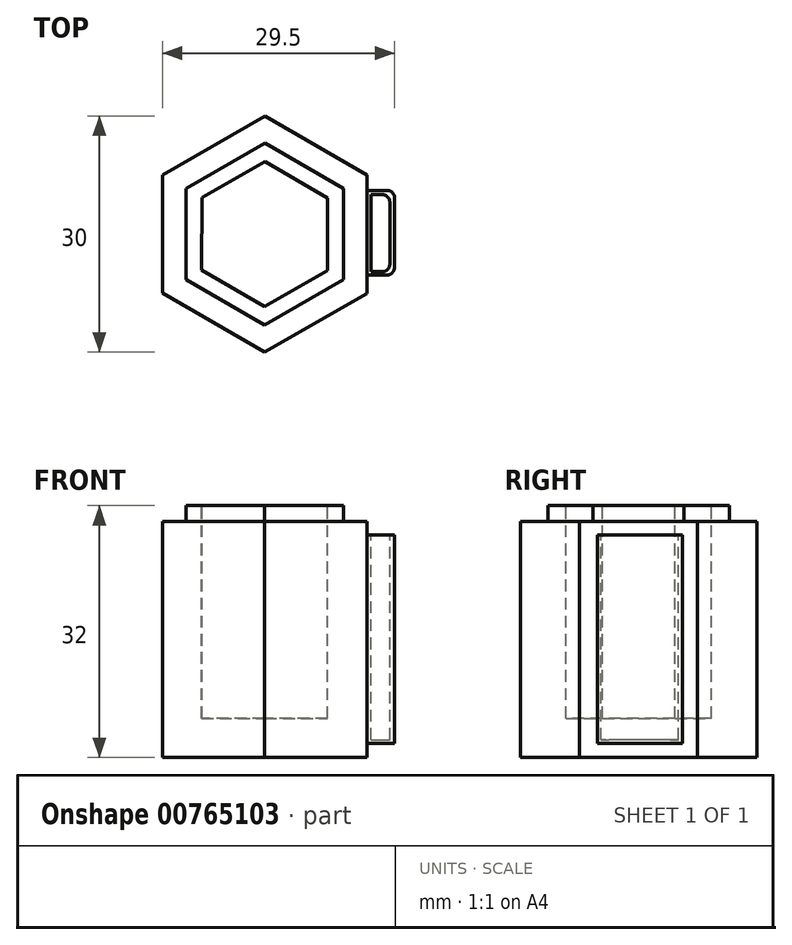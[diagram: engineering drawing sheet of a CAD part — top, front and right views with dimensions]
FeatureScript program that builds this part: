
annotation { "Feature Type Name" : "Feature", "Feature Type Description" : "" }
export const myFeature = defineFeature(function(context is Context, id is Id, definition is map)
    precondition{}
    {
        {
            var Q0;
            Q0=qCreatedBy(makeId("Top.planeOp"),FACE);
            var sketch = newSketch(context, id + "F0", { "sketchPlane" : qUnion([Q0])});
            skCircle(sketch, "E0.cCircle", {"center": v(0, 0) * mm, "radius": 13 * mm, "construction": true});
            skLineSegment(sketch, "E0.0", {"start": v(0.03, 15) * mm, "end": v(13, 7.48) * mm});
            skLineSegment(sketch, "E0.1", {"start": v(13, 7.48) * mm, "end": v(12.98, -7.52) * mm});
            skLineSegment(sketch, "E0.2", {"start": v(12.98, -7.52) * mm, "end": v(-0.03, -15) * mm});
            skLineSegment(sketch, "E0.3", {"start": v(-0.03, -15) * mm, "end": v(-13, -7.48) * mm});
            skLineSegment(sketch, "E0.4", {"start": v(-13, -7.48) * mm, "end": v(-12.98, 7.52) * mm});
            skLineSegment(sketch, "E0.5", {"start": v(-12.98, 7.52) * mm, "end": v(0.03, 15) * mm});
            skPoint(sketch, "E0.0.midPoint", {"position": v(6.52, 11.24) * mm});
            skSolve(sketch);
        }
        {
            var Q0;
            Q0=makeQuery(id+"F0.imprint","IMPRINT",FACE,{"disambiguationData":[TD([[makeQuery(id+"F0.imprint","IMPRINT",EDGE,{"derivedFrom":sQuery(id+"F0.wireOp",EDGE,"E0.0")}),-1.0]])]});
            extrude(context, id + "F1", {"entities" : qUnion([Q0]), "oppositeDirection" : true, "depth" : 30 * mm, "offsetDistance" : 25 * mm});
        }
        {
            var Q0;
            Q0=makeQuery(id+"F1.opExtrude","CAP_FACE",FACE,{"disambiguationData":[OSD([sQuery(id+"F0.wireOp",EDGE,"E0.0"),sQuery(id+"F0.wireOp",EDGE,"E0.1"),sQuery(id+"F0.wireOp",EDGE,"E0.2"),sQuery(id+"F0.wireOp",EDGE,"E0.3"),sQuery(id+"F0.wireOp",EDGE,"E0.4"),sQuery(id+"F0.wireOp",EDGE,"E0.5")])],"isStart":true});
            var sketch = newSketch(context, id + "F2", { "sketchPlane" : qUnion([Q0])});
            skLineSegment(sketch, "E1.0", {"start": v(8, 4.6) * mm, "end": v(7.98, -4.63) * mm});
            skLineSegment(sketch, "E1.1", {"start": v(0.02, 9.23) * mm, "end": v(8, 4.6) * mm});
            skLineSegment(sketch, "E1.2", {"start": v(-7.98, 4.63) * mm, "end": v(0.02, 9.23) * mm});
            skLineSegment(sketch, "E2.0", {"start": v(-8, -4.6) * mm, "end": v(-7.98, 4.63) * mm});
            skLineSegment(sketch, "E2.1", {"start": v(-0.02, -9.23) * mm, "end": v(-8, -4.6) * mm});
            skLineSegment(sketch, "E2.2", {"start": v(7.98, -4.63) * mm, "end": v(-0.02, -9.23) * mm});
            skSolve(sketch);
        }
        {
            var Q0;
            Q0=makeQuery(id+"F2.imprint","IMPRINT",FACE,{"disambiguationData":[TD([[makeQuery(id+"F2.imprint","IMPRINT",EDGE,{"derivedFrom":sQuery(id+"F2.wireOp",EDGE,"E1.0")}),-1.0]])]});
            extrude(context, id + "F3", {"entities" : qUnion([Q0]), "operationType" : NewBodyOperationType.REMOVE, "oppositeDirection" : true, "depth" : 25 * mm, "offsetDistance" : 25 * mm});
        }
        {
            var Q0;
            Q0=makeQuery(id+"F1.opExtrude","CAP_FACE",FACE,{"disambiguationData":[OSD([sQuery(id+"F0.wireOp",EDGE,"E0.0"),sQuery(id+"F0.wireOp",EDGE,"E0.1"),sQuery(id+"F0.wireOp",EDGE,"E0.2"),sQuery(id+"F0.wireOp",EDGE,"E0.3"),sQuery(id+"F0.wireOp",EDGE,"E0.4"),sQuery(id+"F0.wireOp",EDGE,"E0.5")])],"isStart":true});
            var sketch = newSketch(context, id + "F4", { "sketchPlane" : qUnion([Q0])});
            skLineSegment(sketch, "E3.0", {"start": v(-10, -5.75) * mm, "end": v(-9.98, 5.79) * mm});
            skLineSegment(sketch, "E3.1", {"start": v(0.02, 11.54) * mm, "end": v(10, 5.75) * mm});
            skLineSegment(sketch, "E3.2", {"start": v(10, 5.75) * mm, "end": v(9.98, -5.79) * mm});
            skLineSegment(sketch, "E3.3", {"start": v(-9.98, 5.79) * mm, "end": v(0.02, 11.54) * mm});
            skLineSegment(sketch, "E3.4", {"start": v(9.98, -5.79) * mm, "end": v(-0.02, -11.54) * mm});
            skLineSegment(sketch, "E3.5", {"start": v(-0.02, -11.54) * mm, "end": v(-10, -5.75) * mm});
            skSolve(sketch);
        }
        {
            var Q0;
            Q0=makeQuery(id+"F4.imprint","IMPRINT",FACE,{"disambiguationData":[TD([[makeQuery(id+"F4.imprint","IMPRINT",EDGE,{"derivedFrom":sQuery(id+"F4.wireOp",EDGE,"E3.0")}),-1.0]])]});
            extrude(context, id + "F5", {"entities" : qUnion([Q0]), "operationType" : NewBodyOperationType.ADD, "depth" : 2 * mm, "offsetDistance" : 25 * mm});
        }
        {
            var Q0;
            Q0=makeQuery(id+"F1.opExtrude","SWEPT_FACE",FACE,{"disambiguationData":[OSD([sQuery(id+"F0.wireOp",EDGE,"E0.1")])]});
            var sketch = newSketch(context, id + "F6", { "sketchPlane" : qUnion([Q0])});
            skLineSegment(sketch, "E4.bottom", {"start": v(-5.2, -28.18) * mm, "end": v(5.57, -28.18) * mm});
            skLineSegment(sketch, "E4.top", {"start": v(-5.2, -1.74) * mm, "end": v(5.57, -1.74) * mm});
            skLineSegment(sketch, "E4.left", {"start": v(-5.2, -28.18) * mm, "end": v(-5.2, -1.74) * mm});
            skLineSegment(sketch, "E4.right", {"start": v(5.57, -28.18) * mm, "end": v(5.57, -1.74) * mm});
            skLineSegment(sketch, "E5", {"start": v(0, 23.65) * mm, "end": v(0, -57.44) * mm, "construction": true});
            skPoint(sketch, "E5.startSnap0", {"position": v(0, 0) * mm});
            skSolve(sketch);
        }
        {
            var Q0;
            Q0=makeQuery(id+"F6.imprint","IMPRINT",FACE,{"disambiguationData":[TD([[makeQuery(id+"F6.imprint","IMPRINT",EDGE,{"derivedFrom":sQuery(id+"F6.wireOp",EDGE,"E4.bottom")}),1.0]])]});
            extrude(context, id + "F7", {"entities" : qUnion([Q0]), "operationType" : NewBodyOperationType.ADD, "depth" : 3.5 * mm, "offsetDistance" : 25 * mm});
        }
        {
            var Q0;
            Q0=makeQuery(id+"F7.opExtrude","SWEPT_FACE",FACE,{"disambiguationData":[OSD([sQuery(id+"F6.wireOp",EDGE,"E4.top")])]});
            var sketch = newSketch(context, id + "F8", { "sketchPlane" : qUnion([Q0])});
            skLineSegment(sketch, "E6.bottom", {"start": v(13.51, 5.02) * mm, "end": v(15.9, 5.02) * mm});
            skLineSegment(sketch, "E6.top", {"start": v(13.51, -4.8) * mm, "end": v(15.9, -4.8) * mm});
            skLineSegment(sketch, "E6.left", {"start": v(13.51, 5.02) * mm, "end": v(13.51, -4.8) * mm});
            skLineSegment(sketch, "E6.right", {"start": v(15.9, 5.02) * mm, "end": v(15.9, -4.8) * mm});
            skSolve(sketch);
        }
        {
            var Q0;
            Q0=makeQuery(id+"F8.imprint","IMPRINT",FACE,{"disambiguationData":[TD([[makeQuery(id+"F8.imprint","IMPRINT",EDGE,{"derivedFrom":sQuery(id+"F8.wireOp",EDGE,"E6.bottom")}),-1.0]])]});
            extrude(context, id + "F9", {"entities" : qUnion([Q0]), "operationType" : NewBodyOperationType.REMOVE, "oppositeDirection" : true, "depth" : 26 * mm, "offsetDistance" : 25 * mm});
        }
        {
            var Q0;
            Q0=makeQuery(id+"F7.opExtrude","CAP_EDGE",EDGE,{"disambiguationData":[OSD([sQuery(id+"F6.wireOp",EDGE,"E4.left")])],"isStart":false});
            var Q1;
            Q1=makeQuery(id+"F7.opExtrude","CAP_EDGE",EDGE,{"disambiguationData":[OSD([sQuery(id+"F6.wireOp",EDGE,"E4.right")])],"isStart":false});
            var Q2;
            Q2=makeQuery(id+"F9.boolean.opBoolean","COPY",EDGE,{"derivedFrom":makeQuery(id+"F9.opExtrude","SWEPT_EDGE",EDGE,{"disambiguationData":[OSD([sQuery(id+"F8.wireOp",EDGE,"E6.bottom"),sQuery(id+"F8.wireOp",EDGE,"E6.right")])]})});
            var Q3;
            Q3=makeQuery(id+"F9.boolean.opBoolean","COPY",EDGE,{"derivedFrom":makeQuery(id+"F9.opExtrude","SWEPT_EDGE",EDGE,{"disambiguationData":[OSD([sQuery(id+"F8.wireOp",EDGE,"E6.top"),sQuery(id+"F8.wireOp",EDGE,"E6.right")])]})});
            fillet(context, id + "F10", {"entities" : qUnion([Q0, Q1, Q2, Q3]), "radius" : 1 * mm, "tangentPropagation" : true, "allowEdgeOverflow" : false});
        }
    });
